# Revit family: ROBUSTxWSxx
name_source: partatom
category: Leuchten
units: mm (PartAtom-declared; Revit-internal decimal feet)

## family parameters
Basisbauteil = Fläche
Beim Laden mit Abzugskörper schneiden = Nein
Bemaßung runder Anschluss = Durchmesser verwenden
Gemeinsam genutzt = Nein
Lichtquelle = Ja
OmniClass-Nummer = 23.80.70.11
OmniClass-Titel = Luminaries for Internal Lighting
Raumberechnungspunkt = Nein
Teiletyp = Normal

## types (16) — shared parameters
Baugruppenkennzeichen = D5020200
Emissionsform beim Rendern sichtbar = Nein
Farbfilter = 16777215
Farbtemperaturverschiebung bei Dämpfen der Lampe = <Keine Auswahl>
Hersteller = RIDI Leuchten GmbH
Lampe = LED
Neigungswinkel = 90.00°
URL = www.ridi.de
Von Breite des Rechtecks ausssenden = 288 mm  [stored 0.944882 ft]
Von Länge des Rechtecks aussenden = 383 mm  [stored 1.25656 ft]
brand = RIDI
conformity mark = CE
electrical safety class = 1
height = 131 mm  [stored 0.42979 ft]
ingress protection (IP) code = IP66
length = 415 mm  [stored 1.36155 ft]
nominal frequency = 50-60Hz
nominal voltage = 230
voltage type (AC, DC, UC) = AC
weight = 7,2
width = 415 mm  [stored 1.36155 ft]
zero-valued in all types: Vorgabe-Ansicht

## per-type parameters (varying)
| type | Datei für fotometrisches Netz | Modell | Scheinlast | rated input power |
| ROBUST NDWS840B2000 | ROBUST-G2_B.IES | 0627896 | 125 VA | 125 |
| ROBUST NDWS840T2000 | ROBUST-G2_T.IES | 0627897 | 125 VA | 125 |
| ROBUST NDWS840B3000 | ROBUST-G2_B.IES | 0627898 | 195 VA | 195 |
| ROBUST NDWS840T3000 | ROBUST-G2_T.IES | 0627899 | 195 VA | 195 |
| ROBUST NDWS865B2000 | ROBUST-G2_B.IES | 0627900 | 125 VA | 125 |
| ROBUST NDWS865T2000 | ROBUST-G2_T.IES | 0627901 | 125 VA | 125 |
| ROBUST NDWS865B3000 | ROBUST-G2_B.IES | 0627902 | 195 VA | 195 |
| ROBUST NDWS865T3000 | ROBUST-G2_T.IES | 0627903 | 195 VA | 195 |
| ROBUST DAWS840B2000 | ROBUST-G2_B.IES | 0637896 | 125 VA | 125 |
| ROBUST DAWS840T2000 | ROBUST-G2_T.IES | 0637897 | 125 VA | 125 |
| ROBUST DAWS840B3000 | ROBUST-G2_B.IES | 0637898 | 195 VA | 195 |
| ROBUST DAWS840T3000 | ROBUST-G2_T.IES | 0637899 | 195 VA | 195 |
| ROBUST DAWS865B2000 | ROBUST-G2_B.IES | 0637900 | 125 VA | 125 |
| ROBUST DAWS865T2000 | ROBUST-G2_T.IES | 0637901 | 125 VA | 125 |
| ROBUST DAWS865B3000 | ROBUST-G2_B.IES | 0637902 | 195 VA | 195 |
| ROBUST DAWS865T3000 | ROBUST-G2_T.IES | 0637903 | 195 VA | 195 |

note: column(s) folded — value = type name in every type: product name

note: [stored X ft] marks values corroborated as IEEE doubles in the binary element streams (Revit-internal decimal feet)
